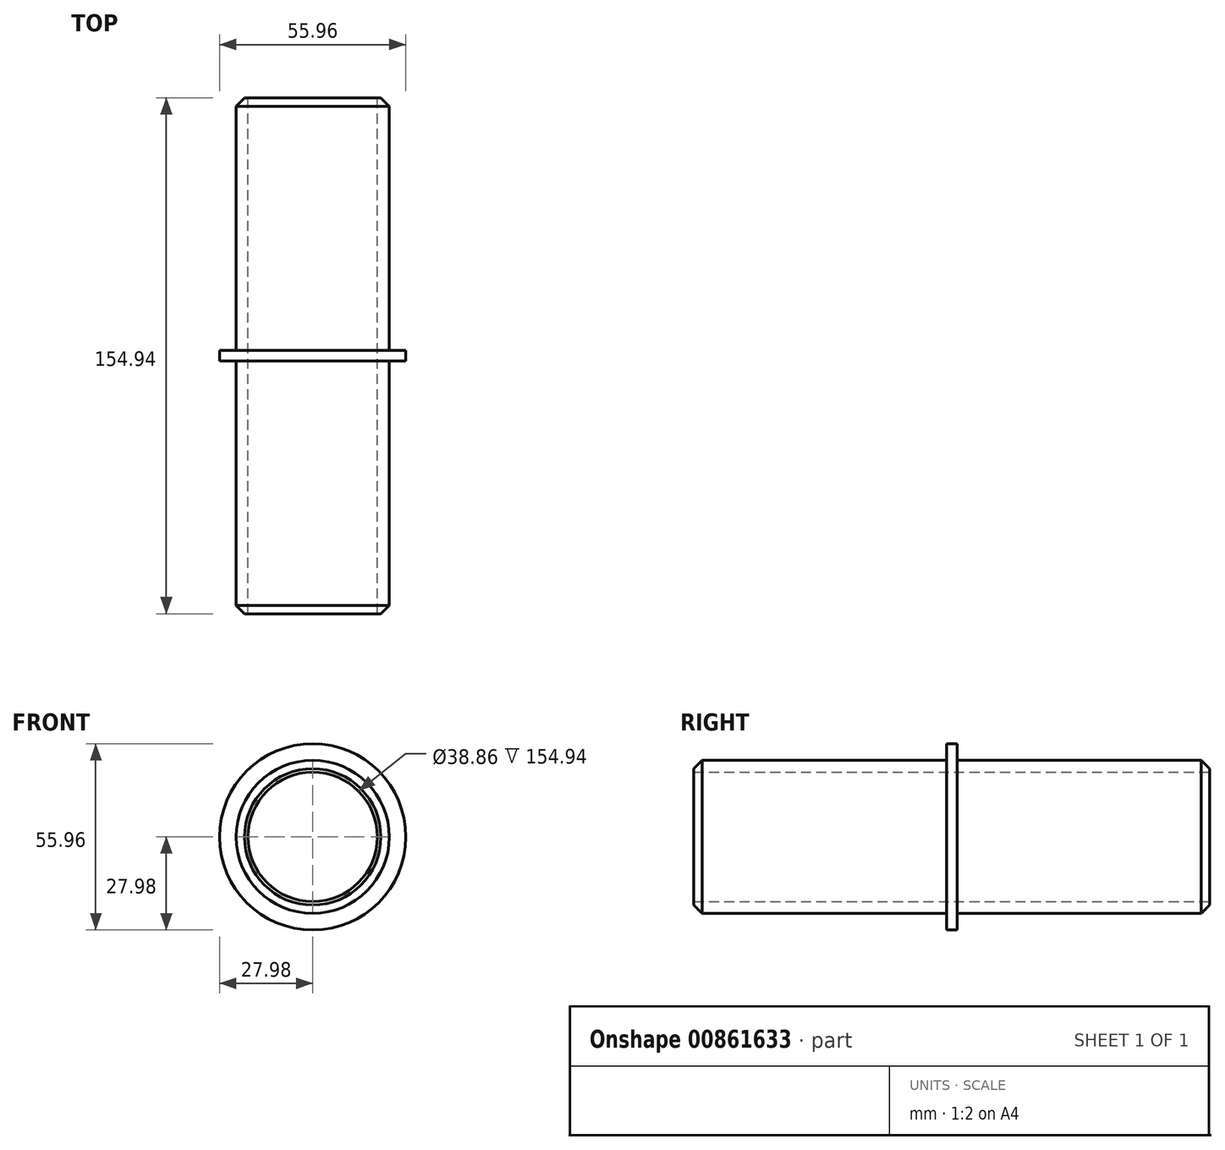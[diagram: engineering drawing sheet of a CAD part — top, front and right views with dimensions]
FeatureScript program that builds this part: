
annotation { "Feature Type Name" : "Feature", "Feature Type Description" : "" }
export const myFeature = defineFeature(function(context is Context, id is Id, definition is map)
    precondition{}
    {
        {
            var Q0;
            Q0=qCreatedBy(makeId("Front.planeOp"),FACE);
            var sketch = newSketch(context, id + "F0", { "sketchPlane" : qUnion([Q0])});
            skCircle(sketch, "E0", {"center": v(0, 0) * mm, "radius": 19.43 * mm});
            skCircle(sketch, "E1", {"center": v(0, 0) * mm, "radius": 23 * mm});
            skCircle(sketch, "E2", {"center": v(0, 0) * mm, "radius": 27.98 * mm});
            skSolve(sketch);
        }
        {
            var Q0;
            Q0=makeQuery(id+"F0.imprint","IMPRINT",FACE,{"disambiguationData":[TD([[makeQuery(id+"F0.imprint","IMPRINT",EDGE,{"derivedFrom":sQuery(id+"F0.wireOp",EDGE,"E0")}),-1.0]])]});
            extrude(context, id + "F1", {"entities" : qUnion([Q0]), "endBound" : BoundingType.SYMMETRIC, "depth" : 154.94 * mm, "offsetDistance" : 25.4 * mm});
        }
        {
            var Q0;
            Q0=makeQuery(id+"F1.opExtrude","CAP_EDGE",EDGE,{"disambiguationData":[OSD([sQuery(id+"F0.wireOp",EDGE,"E1")])],"isStart":false});
            var Q1;
            Q1=makeQuery(id+"F1.opExtrude","CAP_EDGE",EDGE,{"disambiguationData":[OSD([sQuery(id+"F0.wireOp",EDGE,"E1")])],"isStart":true});
            chamfer(context, id + "F2", {"entities" : qUnion([Q0, Q1]), "width" : 2.54 * mm, "tangentPropagation" : true});
        }
        {
            var Q0;
            Q0=makeQuery(id+"F0.imprint","IMPRINT",FACE,{"disambiguationData":[TD([[makeQuery(id+"F0.imprint","IMPRINT",EDGE,{"derivedFrom":sQuery(id+"F0.wireOp",EDGE,"E1")}),-1.0]])]});
            extrude(context, id + "F3", {"entities" : qUnion([Q0]), "operationType" : NewBodyOperationType.ADD, "endBound" : BoundingType.SYMMETRIC, "depth" : 3.17 * mm, "offsetDistance" : 25.4 * mm});
        }
    });
